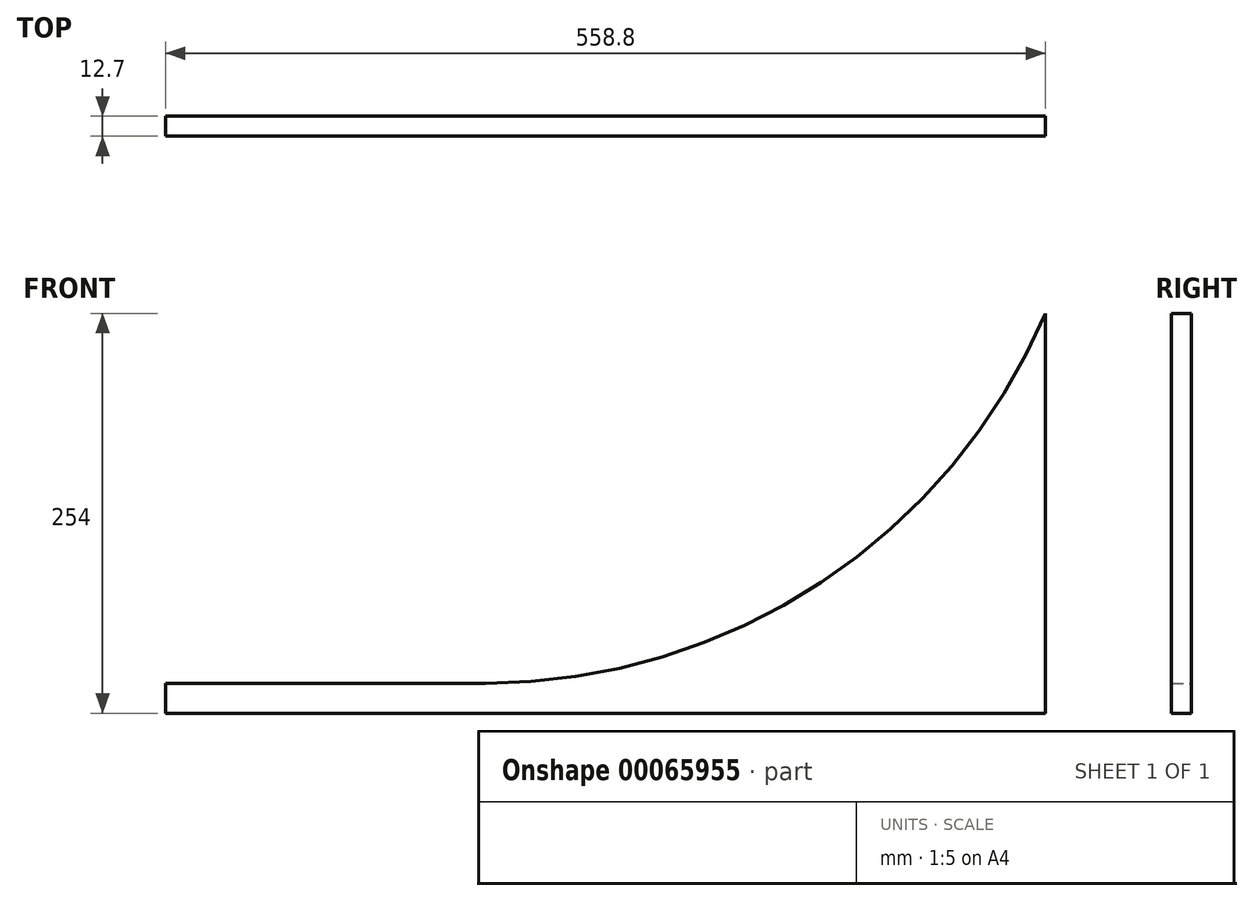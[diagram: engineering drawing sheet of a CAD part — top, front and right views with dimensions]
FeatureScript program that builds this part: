
annotation { "Feature Type Name" : "Feature", "Feature Type Description" : "" }
export const myFeature = defineFeature(function(context is Context, id is Id, definition is map)
    precondition{}
    {
        {
            var Q0;
            Q0=qCreatedBy(makeId("Front.planeOp"),FACE);
            var sketch = newSketch(context, id + "F0", { "sketchPlane" : qUnion([Q0])});
            skLineSegment(sketch, "E0", {"start": v(-558.8, 0) * mm, "end": v(0, 0) * mm});
            skPoint(sketch, "E1.visualSharp", {"position": v(-48.29, 41.79) * mm});
            skArc(sketch, "E1.filletArc", {"start": v(-54.64, 41.79) * mm, "mid": v(-50.15, 43.65) * mm, "end": v(-48.29, 48.14) * mm});
            skLineSegment(sketch, "E2", {"start": v(-558.8, 19.05) * mm, "end": v(-355.6, 19.05) * mm});
            skLineSegment(sketch, "E3", {"start": v(0, 0) * mm, "end": v(0, 254) * mm});
            skArc(sketch, "E4", {"start": v(-355.6, 19.05) * mm, "mid": v(-142.5, 83.1) * mm, "end": v(0, 254) * mm});
            skLineSegment(sketch, "E5", {"start": v(-558.8, 19.05) * mm, "end": v(-558.8, 0) * mm});
            skSolve(sketch);
        }
        {
            var Q0;
            Q0=makeQuery(id+"F0.imprint","IMPRINT",FACE,{"disambiguationData":[TD([[makeQuery(id+"F0.imprint","IMPRINT",EDGE,{"derivedFrom":sQuery(id+"F0.wireOp",EDGE,"E0")}),1.0]])]});
            extrude(context, id + "F1", {"entities" : qUnion([Q0]), "depth" : 12.7 * mm});
        }
    });
